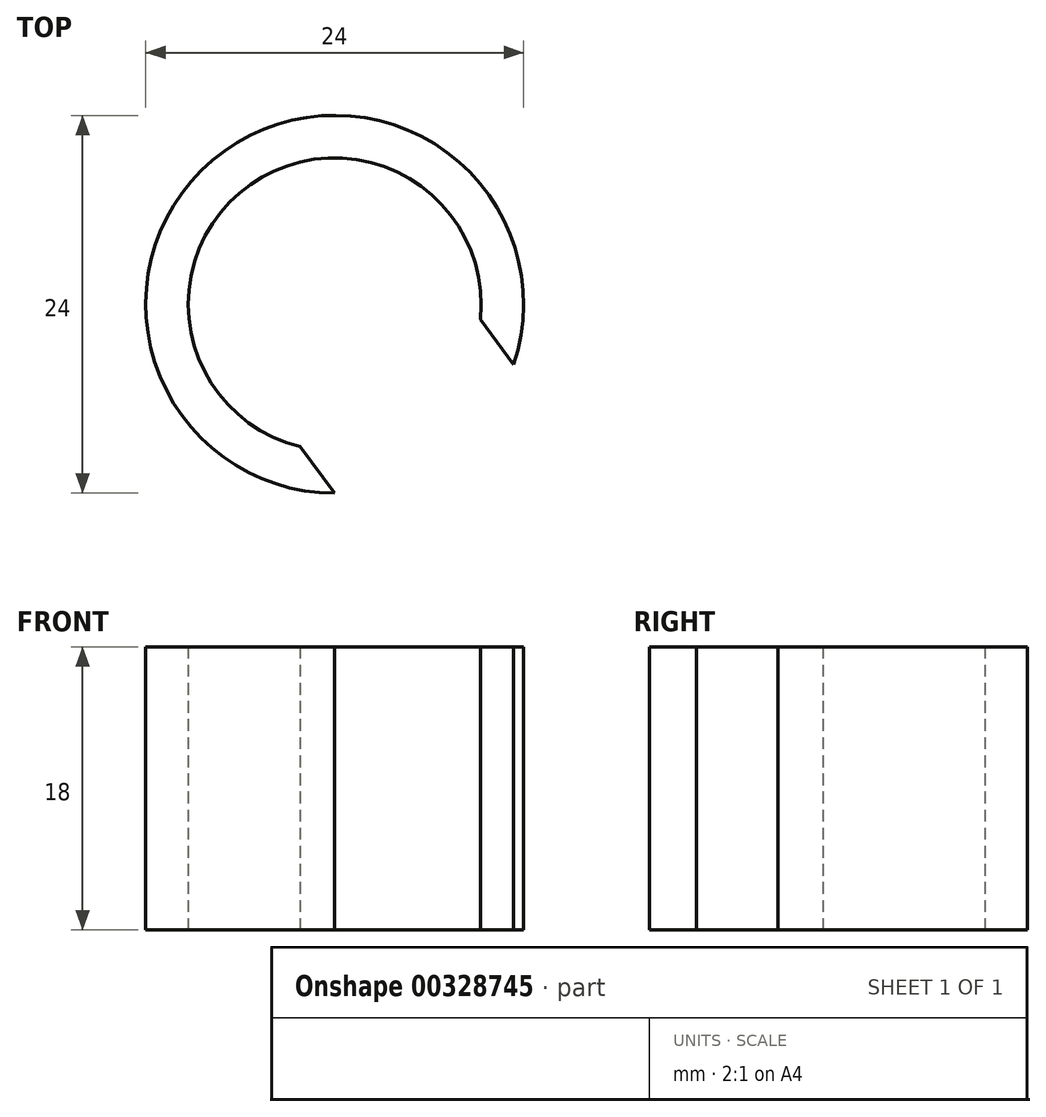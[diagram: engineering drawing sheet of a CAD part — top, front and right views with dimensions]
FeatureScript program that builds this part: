
annotation { "Feature Type Name" : "Feature", "Feature Type Description" : "" }
export const myFeature = defineFeature(function(context is Context, id is Id, definition is map)
    precondition{}
    {
        {
            var Q0;
            Q0=qCreatedBy(makeId("Top.planeOp"),FACE);
            var sketch = newSketch(context, id + "F0", { "sketchPlane" : qUnion([Q0])});
            skArc(sketch, "E0", {"start": v(9.25, -0.98) * mm, "mid": v(-5.35, 7.6) * mm, "end": v(-2.2, -9.03) * mm});
            skArc(sketch, "E1", {"start": v(11.37, -3.83) * mm, "mid": v(-7, 9.75) * mm, "end": v(0, -12) * mm});
            skLineSegment(sketch, "E2", {"start": v(11.37, -3.83) * mm, "end": v(9.25, -0.98) * mm});
            skLineSegment(sketch, "E3", {"start": v(0, -12) * mm, "end": v(-2.2, -9.03) * mm});
            skLineSegment(sketch, "E4", {"start": v(3.05, -16.1) * mm, "end": v(14.42, -7.93) * mm, "construction": true});
            skLineSegment(sketch, "E5", {"start": v(0, -12) * mm, "end": v(11.37, -3.83) * mm, "construction": true});
            skSolve(sketch);
        }
        {
            var Q0;
            Q0 = qSketchRegion(id + "F0", true);
            extrude(context, id + "F1", {"entities" : qUnion([Q0]), "depth" : 18 * mm});
        }
    });
